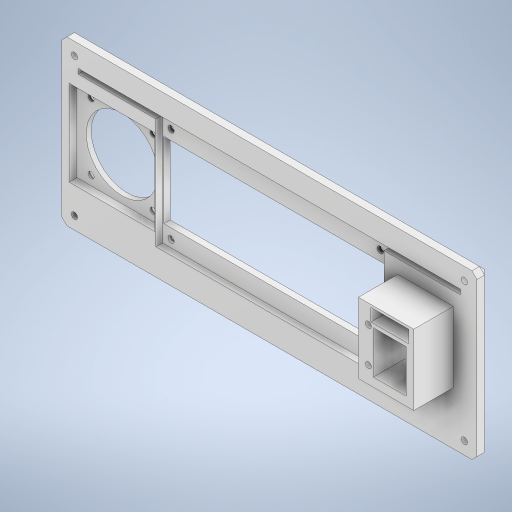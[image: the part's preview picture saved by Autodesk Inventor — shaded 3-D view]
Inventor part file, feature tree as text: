
AUTODESK INVENTOR PART (.ipt)
format: ipt  version: 2024.2 (Build 282272000, 272)  size: 417,792 bytes
history: native  units: in
note: dims shown in document units (in); Inventor stores cm internally (conversion verified against a paired STEP export)
features: extrude x9, chamfer x4, sketch x3
ambient origin geometry x8: Origin, YZ Plane, XZ Plane, XY Plane, X Axis, Y Axis, Z Axis, Center Point
bodies: Solide1 (feature_tree)
feature tree (16):
  sketch  "Esquisse1"
  extrude  "Extrusion1"  Depth=6.4961in
  extrude  "Extrusion2"  Depth=2.5591in
  chamfer  "Chanfrein1"  Distance=1.1811in
  extrude  "Extrusion3"  Depth=3.5039in
  extrude  "Extrusion4"  Depth=3.5118in
  chamfer  "Chanfrein2"  Distance=0.1024in
  extrude  "Extrusion5"  Depth=0.1969in TaperAngle=0.0deg
  chamfer  "Chanfrein3"  Distance=0.0984in
  extrude  "Extrusion6"  Depth=0.0591in TaperAngle=45.0deg
  extrude  "Extrusion7"  Depth=1.3386in
  extrude  "Extrusion8"  Depth=1.3386in
  extrude  "Extrusion10"  Depth=0.0394in
  chamfer  "Chanfrein4"  Distance=0.0984in
  sketch  "Esquisse3"
  sketch  "Esquisse4"
